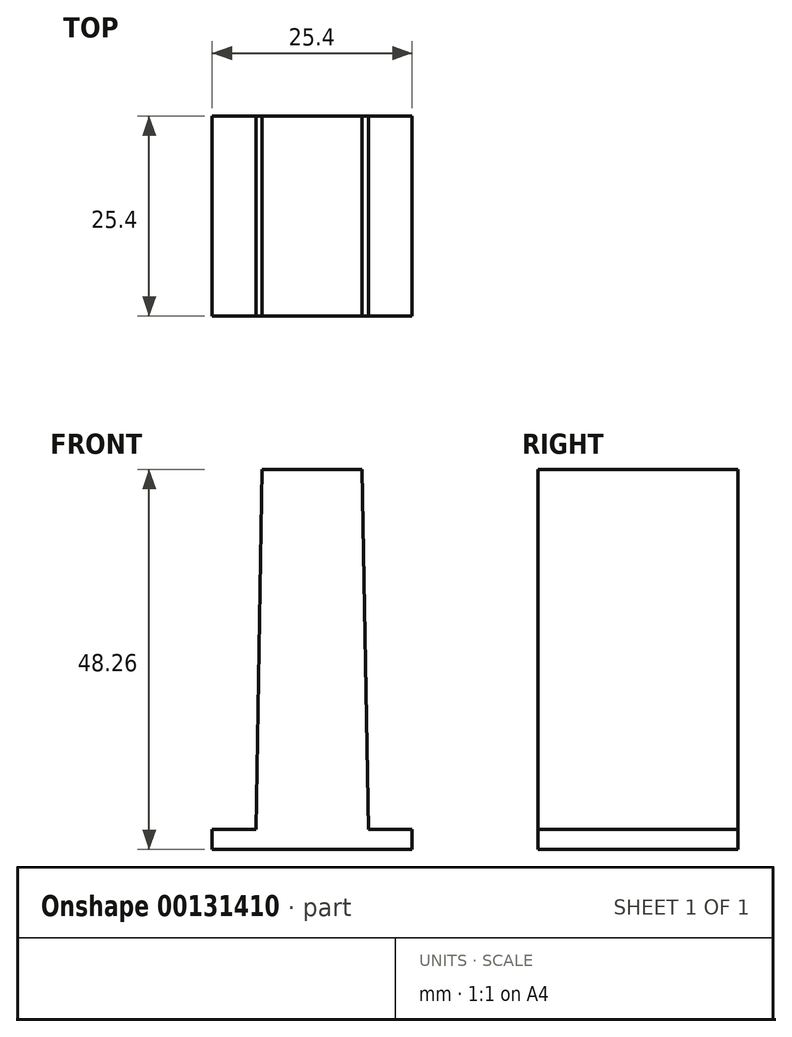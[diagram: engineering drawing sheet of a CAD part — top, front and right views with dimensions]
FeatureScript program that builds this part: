
annotation { "Feature Type Name" : "Feature", "Feature Type Description" : "" }
export const myFeature = defineFeature(function(context is Context, id is Id, definition is map)
    precondition{}
    {
        {
            var Q0;
            Q0=qCreatedBy(makeId("Front.planeOp"),FACE);
            var sketch = newSketch(context, id + "F0", { "sketchPlane" : qUnion([Q0])});
            skLineSegment(sketch, "E0", {"start": v(0, 56.69) * mm, "end": v(0, -59.18) * mm, "construction": true});
            skLineSegment(sketch, "E1", {"start": v(-12.7, 0) * mm, "end": v(-7.15, 0) * mm});
            skLineSegment(sketch, "E2", {"start": v(-7.15, 0) * mm, "end": v(-6.35, 45.72) * mm});
            skLineSegment(sketch, "E3", {"start": v(-6.35, 45.72) * mm, "end": v(0, 45.72) * mm});
            skLineSegment(sketch, "E4", {"start": v(-12.7, 0) * mm, "end": v(-12.7, -2.54) * mm});
            skLineSegment(sketch, "E5", {"start": v(-12.7, -2.54) * mm, "end": v(12.7, -2.54) * mm});
            skLineSegment(sketch, "E6.MirrorCS", {"start": v(6.35, 45.72) * mm, "end": v(0, 45.72) * mm});
            skLineSegment(sketch, "E7.MirrorCS", {"start": v(7.15, 0) * mm, "end": v(6.35, 45.72) * mm});
            skLineSegment(sketch, "E8.MirrorCS", {"start": v(12.7, 0) * mm, "end": v(12.7, -2.54) * mm});
            skLineSegment(sketch, "E9.MirrorCS", {"start": v(12.7, 0) * mm, "end": v(7.15, 0) * mm});
            skSolve(sketch);
        }
        {
            var Q0;
            Q0 = qSketchRegion(id + "F0", true);
            extrude(context, id + "F1", {"entities" : qUnion([Q0]), "depth" : 25.4 * mm});
        }
    });
